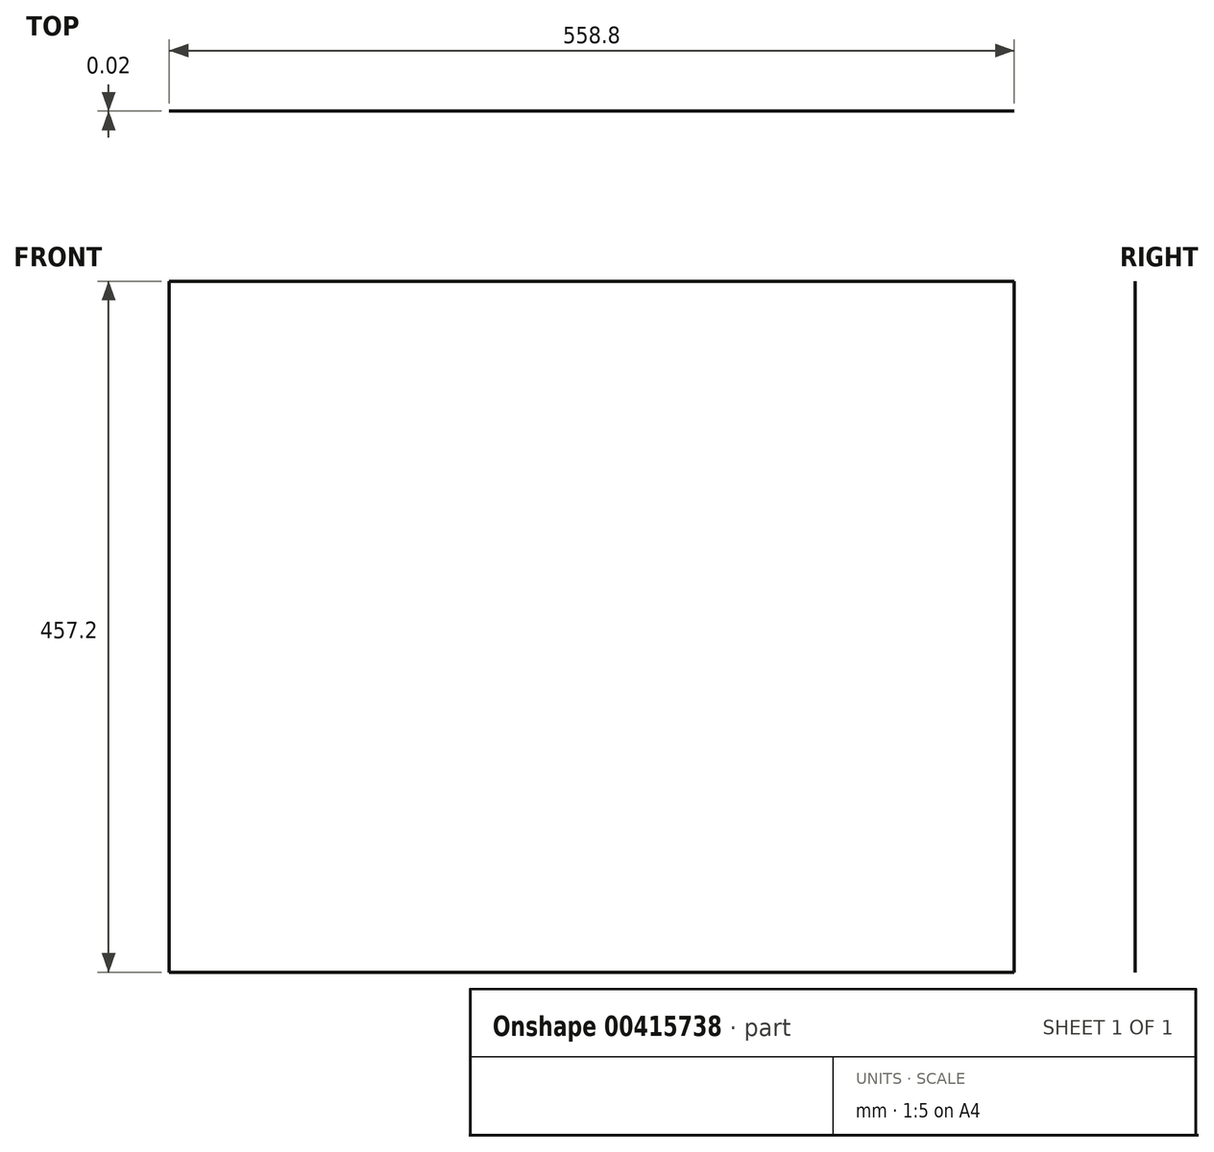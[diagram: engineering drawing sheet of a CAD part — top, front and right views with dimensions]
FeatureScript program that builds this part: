
annotation { "Feature Type Name" : "Feature", "Feature Type Description" : "" }
export const myFeature = defineFeature(function(context is Context, id is Id, definition is map)
    precondition{}
    {
        {
            var Q0;
            Q0=qCreatedBy(makeId("Front.planeOp"),FACE);
            var sketch = newSketch(context, id + "F0", { "sketchPlane" : qUnion([Q0])});
            skLineSegment(sketch, "E0.bottom", {"start": v(279.4, -228.6) * mm, "end": v(-279.4, -228.6) * mm});
            skLineSegment(sketch, "E0.top", {"start": v(279.4, 228.6) * mm, "end": v(-279.4, 228.6) * mm});
            skLineSegment(sketch, "E0.left", {"start": v(279.4, -228.6) * mm, "end": v(279.4, 228.6) * mm});
            skLineSegment(sketch, "E0.right", {"start": v(-279.4, -228.6) * mm, "end": v(-279.4, 228.6) * mm});
            skPoint(sketch, "E0.middle", {"position": v(0, 0) * mm});
            skSolve(sketch);
        }
        {
            var Q0;
            Q0=makeQuery(id+"F0.imprint","IMPRINT",FACE,{"disambiguationData":[TD([[makeQuery(id+"F0.imprint","IMPRINT",EDGE,{"derivedFrom":sQuery(id+"F0.wireOp",EDGE,"E0.bottom")}),-1.0]])]});
            extrude(context, id + "F1", {"entities" : qUnion([Q0]), "depth" : 1 / 50.8 * mm});
        }
    });
